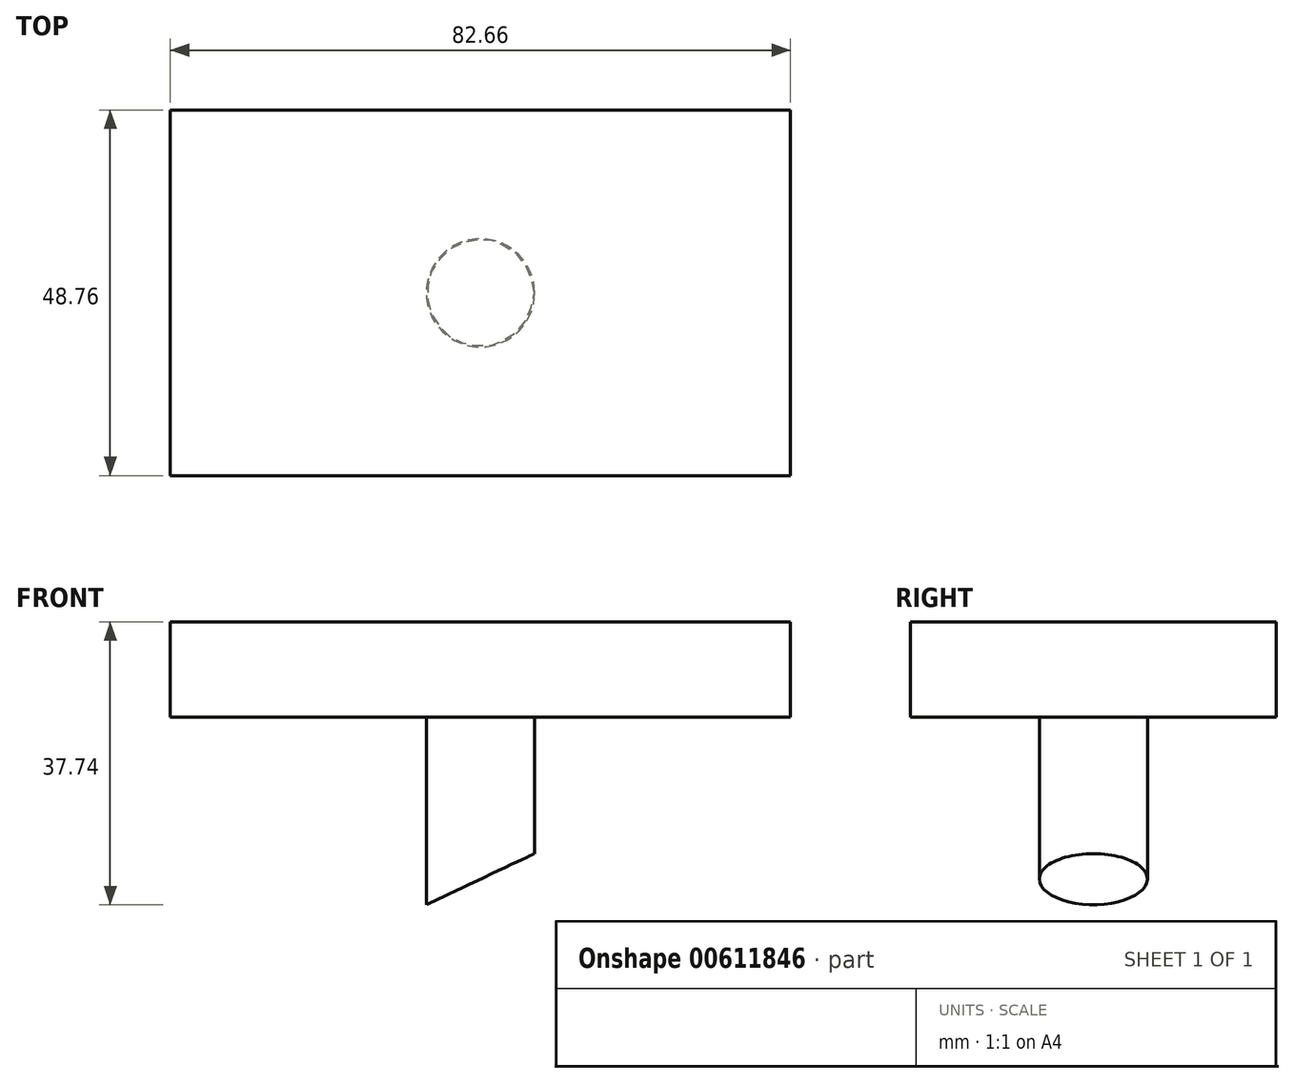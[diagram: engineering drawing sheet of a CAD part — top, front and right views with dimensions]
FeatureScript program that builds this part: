
annotation { "Feature Type Name" : "Feature", "Feature Type Description" : "" }
export const myFeature = defineFeature(function(context is Context, id is Id, definition is map)
    precondition{}
    {
        {
            var Q0;
            Q0=qCreatedBy(makeId("Top.planeOp"),FACE);
            var sketch = newSketch(context, id + "F0", { "sketchPlane" : qUnion([Q0])});
            skLineSegment(sketch, "E0.bottom", {"start": v(-41.33, 24.38) * mm, "end": v(41.33, 24.38) * mm});
            skLineSegment(sketch, "E0.top", {"start": v(-41.33, -24.38) * mm, "end": v(41.33, -24.38) * mm});
            skLineSegment(sketch, "E0.left", {"start": v(-41.33, 24.38) * mm, "end": v(-41.33, -24.38) * mm});
            skLineSegment(sketch, "E0.right", {"start": v(41.33, 24.38) * mm, "end": v(41.33, -24.38) * mm});
            skPoint(sketch, "E0.middle", {"position": v(0, 0) * mm});
            skCircle(sketch, "E1", {"center": v(0, 0) * mm, "radius": 7.2 * mm});
            skSolve(sketch);
        }
        {
            var Q0;
            Q0=makeQuery(id+"F0.imprint","IMPRINT",FACE,{"disambiguationData":[TD([[makeQuery(id+"F0.imprint","IMPRINT",EDGE,{"derivedFrom":sQuery(id+"F0.wireOp",EDGE,"E0.bottom")}),-1.0]])]});
            var Q1;
            Q1=makeQuery(id+"F0.imprint","IMPRINT",FACE,{"disambiguationData":[TD([[makeQuery(id+"F0.imprint","IMPRINT",EDGE,{"derivedFrom":sQuery(id+"F0.wireOp",EDGE,"E1")}),1.0]])]});
            extrude(context, id + "F1", {"entities" : qUnion([Q0, Q1]), "depth" : 12.7 * mm, "offsetDistance" : 25.4 * mm});
        }
        {
            var Q0;
            Q0=makeQuery(id+"F0.imprint","IMPRINT",FACE,{"disambiguationData":[TD([[makeQuery(id+"F0.imprint","IMPRINT",EDGE,{"derivedFrom":sQuery(id+"F0.wireOp",EDGE,"E1")}),1.0]])]});
            var Q1;
            Q1=sQuery(id+"F0.wireOp",EDGE,"E1");
            extrude(context, id + "F2", {"entities" : qUnion([Q0]), "surfaceEntities" : qUnion([Q1]), "oppositeDirection" : true, "depth" : 25.4 * mm, "offsetDistance" : 25.4 * mm});
        }
        {
            var Q0;
            Q0=qCreatedBy(makeId("Front.planeOp"),FACE);
            var sketch = newSketch(context, id + "F3", { "sketchPlane" : qUnion([Q0])});
            skLineSegment(sketch, "E2", {"start": v(-12, -27.31) * mm, "end": v(12.74, -27.31) * mm});
            skLineSegment(sketch, "E3", {"start": v(12.74, -27.31) * mm, "end": v(12.74, -15.58) * mm});
            skLineSegment(sketch, "E4", {"start": v(12.74, -15.58) * mm, "end": v(-12, -27.31) * mm});
            skSolve(sketch);
        }
        {
            var Q0;
            Q0 = qSketchRegion(id + "F3", true);
            extrude(context, id + "F4", {"entities" : qUnion([Q0]), "operationType" : NewBodyOperationType.REMOVE, "endBound" : BoundingType.SYMMETRIC, "oppositeDirection" : true, "depth" : 25.4 * mm, "offsetDistance" : 25.4 * mm});
        }
    });
